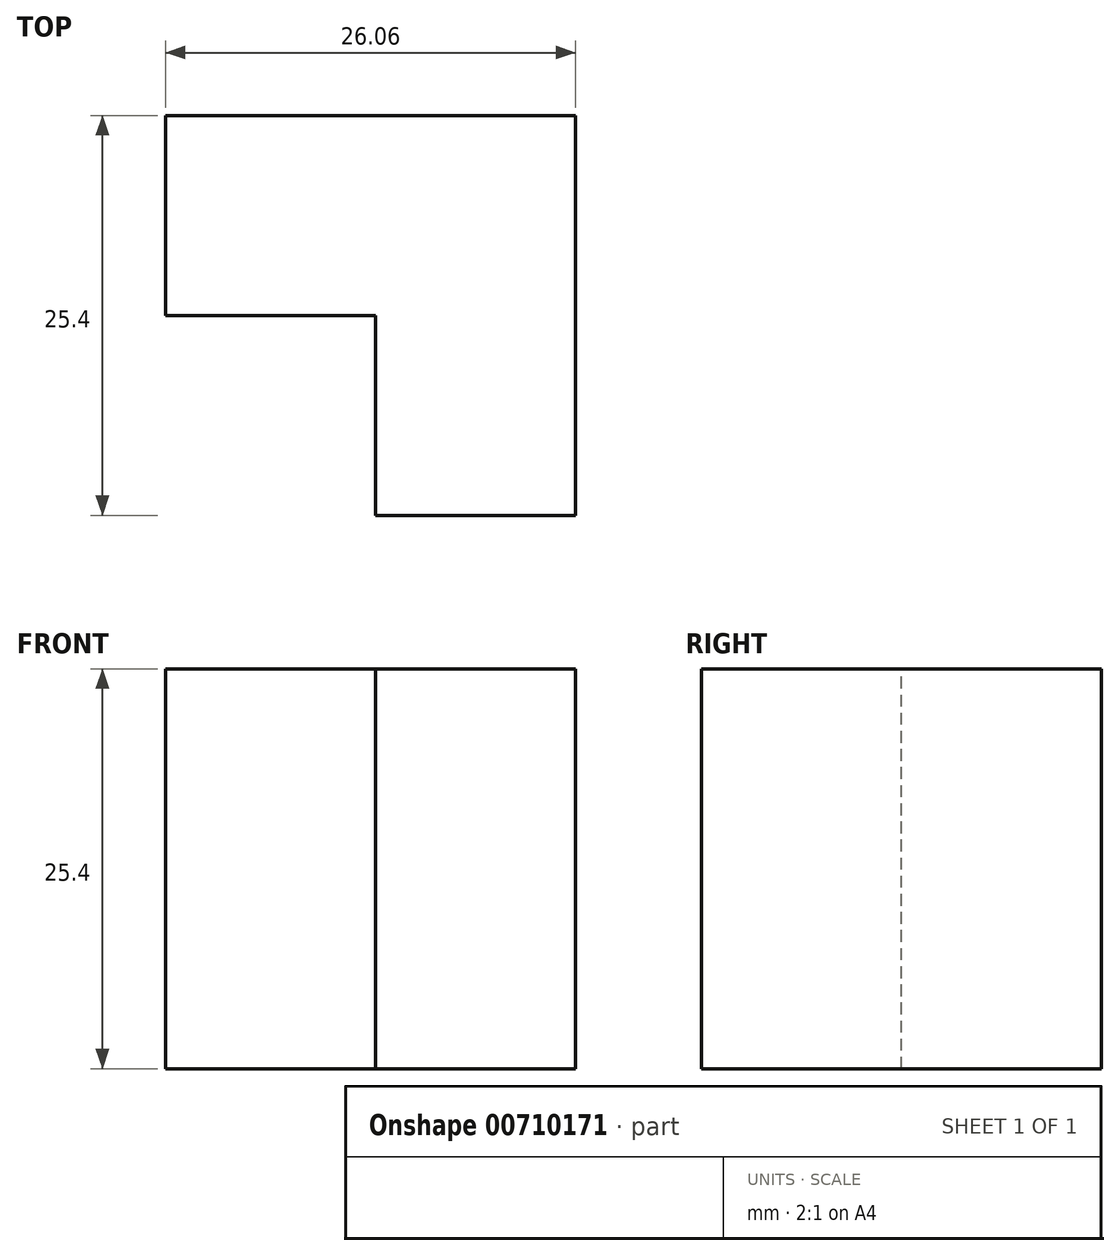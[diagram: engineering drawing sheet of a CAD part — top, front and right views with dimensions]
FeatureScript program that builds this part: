
annotation { "Feature Type Name" : "Feature", "Feature Type Description" : "" }
export const myFeature = defineFeature(function(context is Context, id is Id, definition is map)
    precondition{}
    {
        {
            var Q0;
            Q0=qCreatedBy(makeId("Top.planeOp"),FACE);
            var sketch = newSketch(context, id + "F0", { "sketchPlane" : qUnion([Q0])});
            skLineSegment(sketch, "E0.bottom", {"start": v(0, 0) * mm, "end": v(-26.06, 0) * mm});
            skLineSegment(sketch, "E0.top", {"start": v(-12.7, -12.7) * mm, "end": v(-26.06, -12.7) * mm});
            skLineSegment(sketch, "E0.right", {"start": v(-26.06, 0) * mm, "end": v(-26.06, -12.7) * mm});
            skLineSegment(sketch, "E1.top", {"start": v(0, -25.4) * mm, "end": v(-12.7, -25.4) * mm});
            skLineSegment(sketch, "E1.right", {"start": v(-12.7, -12.7) * mm, "end": v(-12.7, -25.4) * mm});
            skLineSegment(sketch, "E2", {"start": v(0, 0) * mm, "end": v(0, -25.4) * mm});
            skSolve(sketch);
        }
        {
            var Q0;
            Q0=makeQuery(id+"F0.imprint","IMPRINT",FACE,{"disambiguationData":[TD([[makeQuery(id+"F0.imprint","IMPRINT",EDGE,{"derivedFrom":sQuery(id+"F0.wireOp",EDGE,"E0.bottom")}),1.0]])]});
            extrude(context, id + "F1", {"entities" : qUnion([Q0]), "oppositeDirection" : true, "depth" : 25.4 * mm, "offsetDistance" : 25.4 * mm});
        }
    });
